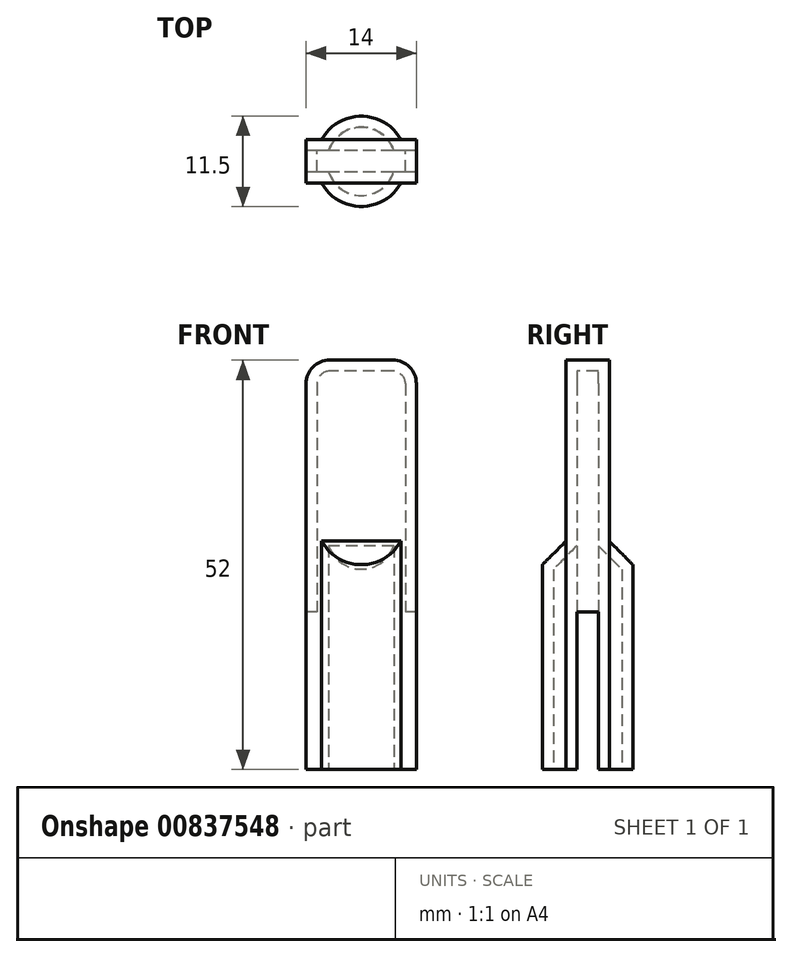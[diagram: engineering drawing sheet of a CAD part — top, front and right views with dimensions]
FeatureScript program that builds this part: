
annotation { "Feature Type Name" : "Feature", "Feature Type Description" : "" }
export const myFeature = defineFeature(function(context is Context, id is Id, definition is map)
    precondition{}
    {
        {
            var Q0;
            Q0=qCreatedBy(makeId("Top.planeOp"),FACE);
            var sketch = newSketch(context, id + "F0", { "sketchPlane" : qUnion([Q0])});
            skCircle(sketch, "E0", {"center": v(0, 0) * mm, "radius": 5.75 * mm});
            skSolve(sketch);
        }
        {
            var Q0;
            Q0 = qSketchRegion(id + "F0", true);
            extrude(context, id + "F1", {"entities" : qUnion([Q0]), "depth" : 26 * mm, "offsetDistance" : 25.4 * mm});
        }
        {
            var Q0;
            Q0=makeQuery(id+"F1.opExtrude","CAP_FACE",FACE,{"disambiguationData":[OSD([sQuery(id+"F0.wireOp",EDGE,"E0")])],"isStart":true});
            var sketch = newSketch(context, id + "F2", { "sketchPlane" : qUnion([Q0])});
            skSolve(sketch);
        }
        {
            var Q0;
            Q0=makeQuery(id+"F2.imprint","IMPRINT",FACE,{"disambiguationData":[TD([[makeQuery(id+"F2.imprint","IMPRINT",EDGE,{"derivedFrom":makeQuery(id+"F1.opExtrude","CAP_EDGE",EDGE,{"disambiguationData":[OSD([sQuery(id+"F0.wireOp",EDGE,"E0")])],"isStart":true})}),-1.0]])]});
            var sketch = newSketch(context, id + "F3", { "sketchPlane" : qUnion([Q0])});
            skLineSegment(sketch, "E1.bottom", {"start": v(7, -2.75) * mm, "end": v(-7, -2.75) * mm});
            skLineSegment(sketch, "E1.top", {"start": v(7, 2.75) * mm, "end": v(-7, 2.75) * mm});
            skLineSegment(sketch, "E1.left", {"start": v(7, -2.75) * mm, "end": v(7, 2.75) * mm});
            skLineSegment(sketch, "E1.right", {"start": v(-7, -2.75) * mm, "end": v(-7, 2.75) * mm});
            skPoint(sketch, "E1.middle", {"position": v(0, 0) * mm});
            skSolve(sketch);
        }
        {
            var Q0;
            Q0 = qSketchRegion(id + "F3", true);
            extrude(context, id + "F4", {"entities" : qUnion([Q0]), "operationType" : NewBodyOperationType.ADD, "oppositeDirection" : true, "depth" : 52 * mm, "offsetDistance" : 25 * mm});
        }
        {
            var Q0;
            Q0=makeQuery(id+"F4.boolean.opBoolean","INTERSECT",EDGE,{"derivedFrom":[makeQuery(id+"F1.opExtrude","CAP_FACE",FACE,{"disambiguationData":[OSD([sQuery(id+"F0.wireOp",EDGE,"E0")])],"isStart":false}),makeQuery(id+"F4.opExtrude","SWEPT_FACE",FACE,{"disambiguationData":[OSD([sQuery(id+"F3.wireOp",EDGE,"E1.top")])]})]});
            var Q1;
            Q1=makeQuery(id+"F4.boolean.opBoolean","INTERSECT",EDGE,{"derivedFrom":[makeQuery(id+"F1.opExtrude","CAP_FACE",FACE,{"disambiguationData":[OSD([sQuery(id+"F0.wireOp",EDGE,"E0")])],"isStart":false}),makeQuery(id+"F4.opExtrude","SWEPT_FACE",FACE,{"disambiguationData":[OSD([sQuery(id+"F3.wireOp",EDGE,"E1.bottom")])]})]});
            chamfer(context, id + "F5", {"entities" : qUnion([Q0, Q1]), "width" : 3 * mm, "tangentPropagation" : true});
        }
        {
            var Q0;
            Q0=makeQuery(id+"F4.opExtrude","CAP_EDGE",EDGE,{"disambiguationData":[OSD([sQuery(id+"F3.wireOp",EDGE,"E1.left")])],"isStart":false});
            var Q1;
            Q1=makeQuery(id+"F4.opExtrude","CAP_EDGE",EDGE,{"disambiguationData":[OSD([sQuery(id+"F3.wireOp",EDGE,"E1.right")])],"isStart":false});
            fillet(context, id + "F6", {"entities" : qUnion([Q0, Q1]), "radius" : 3 * mm, "tangentPropagation" : true, "allowEdgeOverflow" : false});
        }
        {
            var Q0;
            Q0=makeQuery(id+"F4.boolean.opBoolean","MERGE",FACE,{"derivedFrom":[makeQuery(id+"F1.opExtrude","CAP_FACE",FACE,{"disambiguationData":[OSD([sQuery(id+"F0.wireOp",EDGE,"E0")])],"isStart":true}),makeQuery(id+"F4.opExtrude","CAP_FACE",FACE,{"disambiguationData":[OSD([sQuery(id+"F3.wireOp",EDGE,"E1.bottom"),sQuery(id+"F3.wireOp",EDGE,"E1.top"),sQuery(id+"F3.wireOp",EDGE,"E1.left"),sQuery(id+"F3.wireOp",EDGE,"E1.right")])],"isStart":true})]});
            shell(context, id + "F7", {"entities" : qUnion([Q0]), "thickness" : 1.4 * mm});
        }
        {
            var Q0;
            Q0=makeQuery(id+"F2.imprint","IMPRINT",FACE,{"disambiguationData":[TD([[makeQuery(id+"F2.imprint","IMPRINT",EDGE,{"derivedFrom":makeQuery(id+"F1.opExtrude","CAP_EDGE",EDGE,{"disambiguationData":[OSD([sQuery(id+"F0.wireOp",EDGE,"E0")])],"isStart":true})}),-1.0]])]});
            var sketch = newSketch(context, id + "F8", { "sketchPlane" : qUnion([Q0])});
            skLineSegment(sketch, "E2.bottom", {"start": v(16.41, -1.35) * mm, "end": v(-16.41, -1.35) * mm});
            skLineSegment(sketch, "E2.top", {"start": v(16.41, 1.35) * mm, "end": v(-16.41, 1.35) * mm});
            skLineSegment(sketch, "E2.left", {"start": v(16.41, -1.35) * mm, "end": v(16.41, 1.35) * mm});
            skLineSegment(sketch, "E2.right", {"start": v(-16.41, -1.35) * mm, "end": v(-16.41, 1.35) * mm});
            skPoint(sketch, "E2.middle", {"position": v(0, 0) * mm});
            skSolve(sketch);
        }
        {
            var Q0;
            Q0 = qSketchRegion(id + "F8", true);
            extrude(context, id + "F9", {"entities" : qUnion([Q0]), "operationType" : NewBodyOperationType.REMOVE, "oppositeDirection" : true, "depth" : 20 * mm, "offsetDistance" : 25 * mm});
        }
    });
